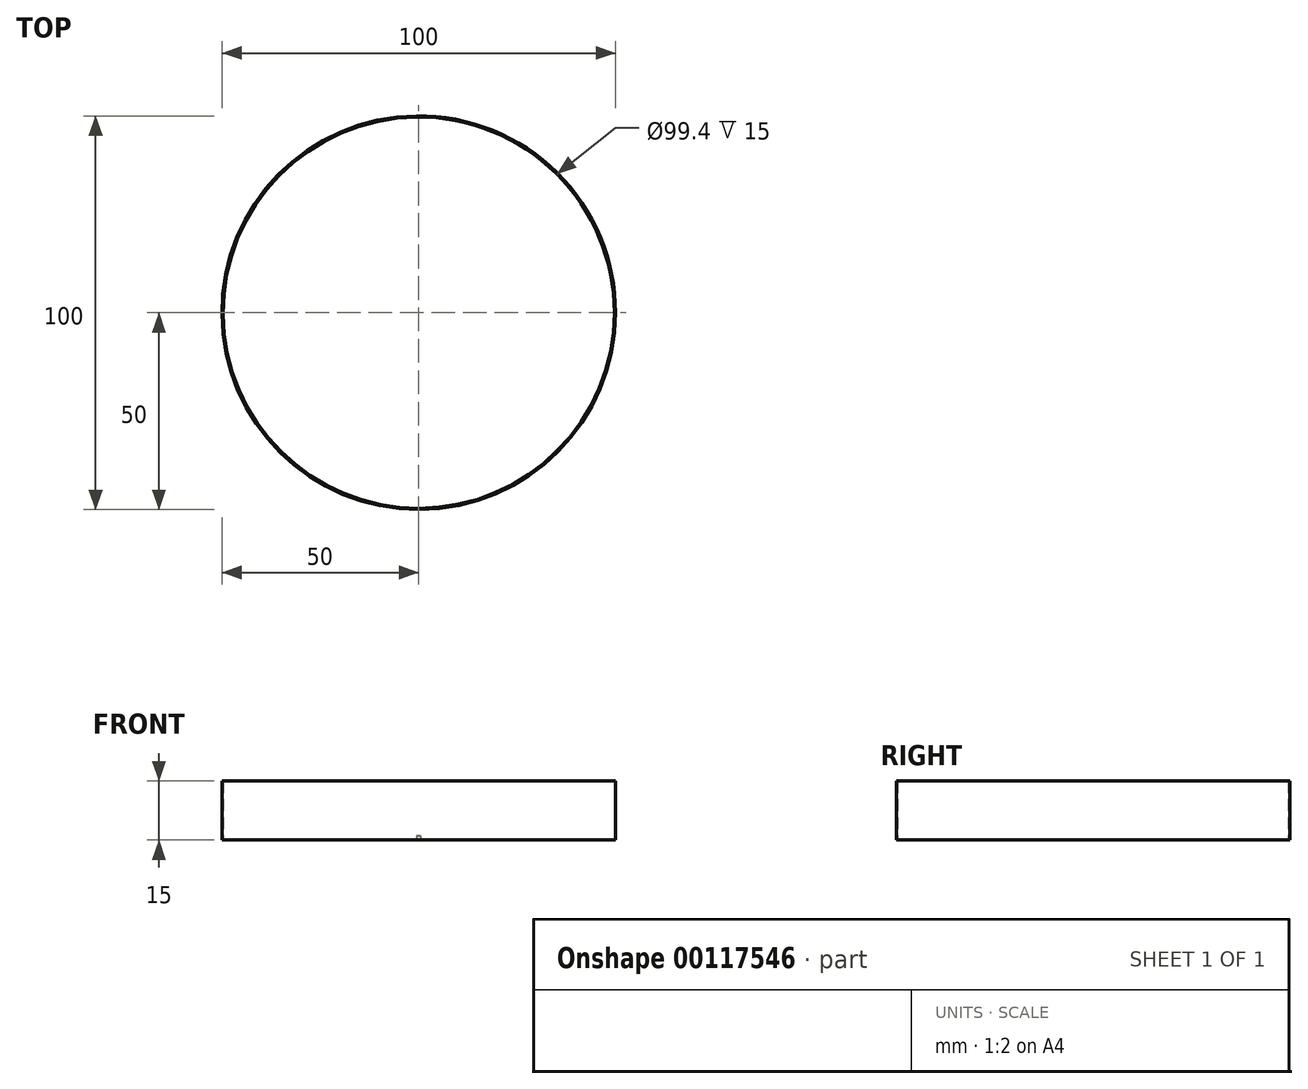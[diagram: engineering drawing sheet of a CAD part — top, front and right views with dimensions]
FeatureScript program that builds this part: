
annotation { "Feature Type Name" : "Feature", "Feature Type Description" : "" }
export const myFeature = defineFeature(function(context is Context, id is Id, definition is map)
    precondition{}
    {
        {
            var Q0;
            Q0=qCreatedBy(makeId("Top.planeOp"),FACE);
            var sketch = newSketch(context, id + "F0", { "sketchPlane" : qUnion([Q0])});
            skCircle(sketch, "E0", {"center": v(0, 0) * mm, "radius": 50 * mm});
            skCircle(sketch, "E1", {"center": v(0, 0) * mm, "radius": 49.7 * mm});
            skSolve(sketch);
        }
        {
            var Q0;
            Q0 = qSketchRegion(id + "F0", true);
            extrude(context, id + "F1", {"entities" : qUnion([Q0]), "depth" : 15 * mm});
        }
        {
            var Q0;
            Q0=qCreatedBy(makeId("Top.planeOp"),FACE);
            var sketch = newSketch(context, id + "F2", { "sketchPlane" : qUnion([Q0])});
            skLineSegment(sketch, "E2.bottom", {"start": v(-0.5, 50) * mm, "end": v(0.5, 50) * mm});
            skLineSegment(sketch, "E2.top", {"start": v(-0.5, 0) * mm, "end": v(0.5, 0) * mm});
            skLineSegment(sketch, "E2.left", {"start": v(-0.5, 50) * mm, "end": v(-0.5, 0) * mm});
            skLineSegment(sketch, "E2.right", {"start": v(0.5, 50) * mm, "end": v(0.5, 0) * mm});
            skSolve(sketch);
        }
        {
            var Q0;
            Q0 = qSketchRegion(id + "F2", true);
            extrude(context, id + "F3", {"entities" : qUnion([Q0]), "operationType" : NewBodyOperationType.REMOVE, "depth" : 1 * mm});
        }
    });
